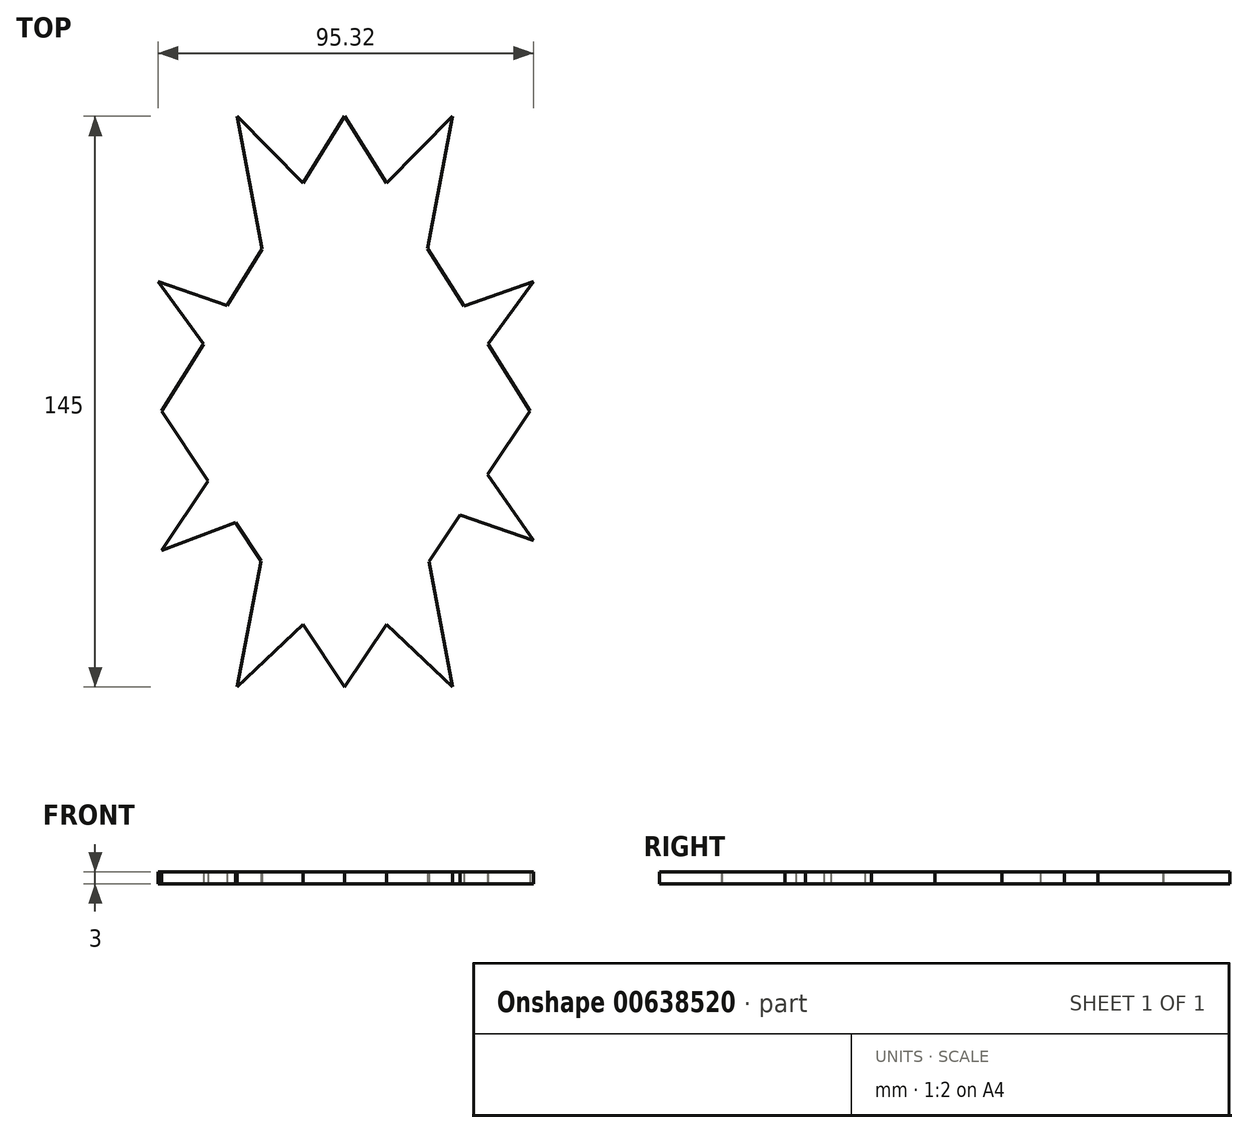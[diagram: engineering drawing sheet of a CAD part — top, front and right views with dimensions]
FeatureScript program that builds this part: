
annotation { "Feature Type Name" : "Feature", "Feature Type Description" : "" }
export const myFeature = defineFeature(function(context is Context, id is Id, definition is map)
    precondition{}
    {
        {
            var Q0;
            Q0=qCreatedBy(makeId("Top.planeOp"),FACE);
            var sketch = newSketch(context, id + "F0", { "sketchPlane" : qUnion([Q0])});
            skLineSegment(sketch, "E0", {"start": v(-46.45, 0) * mm, "end": v(-34.67, -17.76) * mm});
            skLineSegment(sketch, "E1", {"start": v(0, 74.96) * mm, "end": v(-10.5, 58.03) * mm});
            skLineSegment(sketch, "E2", {"start": v(0, 74.96) * mm, "end": v(10.7, 57.94) * mm});
            skLineSegment(sketch, "E3", {"start": v(0, -70.04) * mm, "end": v(10.7, -54.14) * mm});
            skLineSegment(sketch, "E4", {"start": v(47.98, 32.9) * mm, "end": v(36.4, 17.04) * mm});
            skLineSegment(sketch, "E5", {"start": v(-46.45, -35.34) * mm, "end": v(-34.67, -17.76) * mm});
            skLineSegment(sketch, "E6", {"start": v(47.98, -32.9) * mm, "end": v(36.27, -16.1) * mm});
            skLineSegment(sketch, "E7", {"start": v(-47.34, 32.9) * mm, "end": v(-35.86, 17.1) * mm});
            skLineSegment(sketch, "E8.trimOffspring", {"start": v(-27.29, -6.68) * mm, "end": v(-27.29, -6.75) * mm});
            skLineSegment(sketch, "E9", {"start": v(-27.29, 74.96) * mm, "end": v(-20.93, 41.18) * mm});
            skLineSegment(sketch, "E10.trimOffspring", {"start": v(36.27, -16.1) * mm, "end": v(47.1, 0) * mm});
            skLineSegment(sketch, "E11", {"start": v(27.49, 74.96) * mm, "end": v(21.11, 41.35) * mm});
            skLineSegment(sketch, "E12", {"start": v(27.49, 74.96) * mm, "end": v(10.7, 57.94) * mm});
            skLineSegment(sketch, "E13", {"start": v(-27.29, 74.96) * mm, "end": v(-10.5, 58.03) * mm});
            skLineSegment(sketch, "E14.trimOffspring", {"start": v(-20.93, 41.18) * mm, "end": v(-29.85, 26.8) * mm});
            skLineSegment(sketch, "E15.trimOffspring", {"start": v(-29.85, 26.8) * mm, "end": v(-47.34, 32.9) * mm});
            skLineSegment(sketch, "E16.trimOffspring", {"start": v(21.11, 41.35) * mm, "end": v(30.3, 26.73) * mm});
            skLineSegment(sketch, "E17.trimOffspring", {"start": v(21.44, -38.15) * mm, "end": v(27.49, -70.04) * mm});
            skLineSegment(sketch, "E18.trimOffspring", {"start": v(30.3, 26.73) * mm, "end": v(47.98, 32.9) * mm});
            skLineSegment(sketch, "E19.trimOffspring", {"start": v(29.34, -26.4) * mm, "end": v(47.98, -32.9) * mm});
            skLineSegment(sketch, "E20.trimOffspring", {"start": v(36.4, 17.04) * mm, "end": v(47.1, 0) * mm});
            skLineSegment(sketch, "E21.trimOffspring", {"start": v(-35.86, 17.1) * mm, "end": v(-46.45, 0) * mm});
            skLineSegment(sketch, "E22.trimOffspring", {"start": v(-21.26, -38) * mm, "end": v(-27.29, -70.04) * mm});
            skLineSegment(sketch, "E23.trimOffspring", {"start": v(-10.5, -54.23) * mm, "end": v(0, -70.04) * mm});
            skLineSegment(sketch, "E24.trimOffspring", {"start": v(10.7, -54.14) * mm, "end": v(27.49, -70.04) * mm});
            skLineSegment(sketch, "E25.trimOffspring", {"start": v(-10.5, -54.23) * mm, "end": v(-27.29, -70.04) * mm});
            skLineSegment(sketch, "E26", {"start": v(29.34, -26.4) * mm, "end": v(21.44, -38.15) * mm});
            skLineSegment(sketch, "E27", {"start": v(-46.45, -35.34) * mm, "end": v(-27.71, -28.26) * mm});
            skLineSegment(sketch, "E28", {"start": v(-21.26, -38) * mm, "end": v(-27.71, -28.26) * mm});
            skSolve(sketch);
        }
        {
            var Q0;
            Q0=makeQuery(id+"F0.imprint","IMPRINT",FACE,{"disambiguationData":[TD([[makeQuery(id+"F0.imprint","IMPRINT",EDGE,{"derivedFrom":sQuery(id+"F0.wireOp",EDGE,"E0")}),1.0]])]});
            extrude(context, id + "F1", {"entities" : qUnion([Q0]), "depth" : 3 * mm, "offsetDistance" : 25 * mm});
        }
    });
